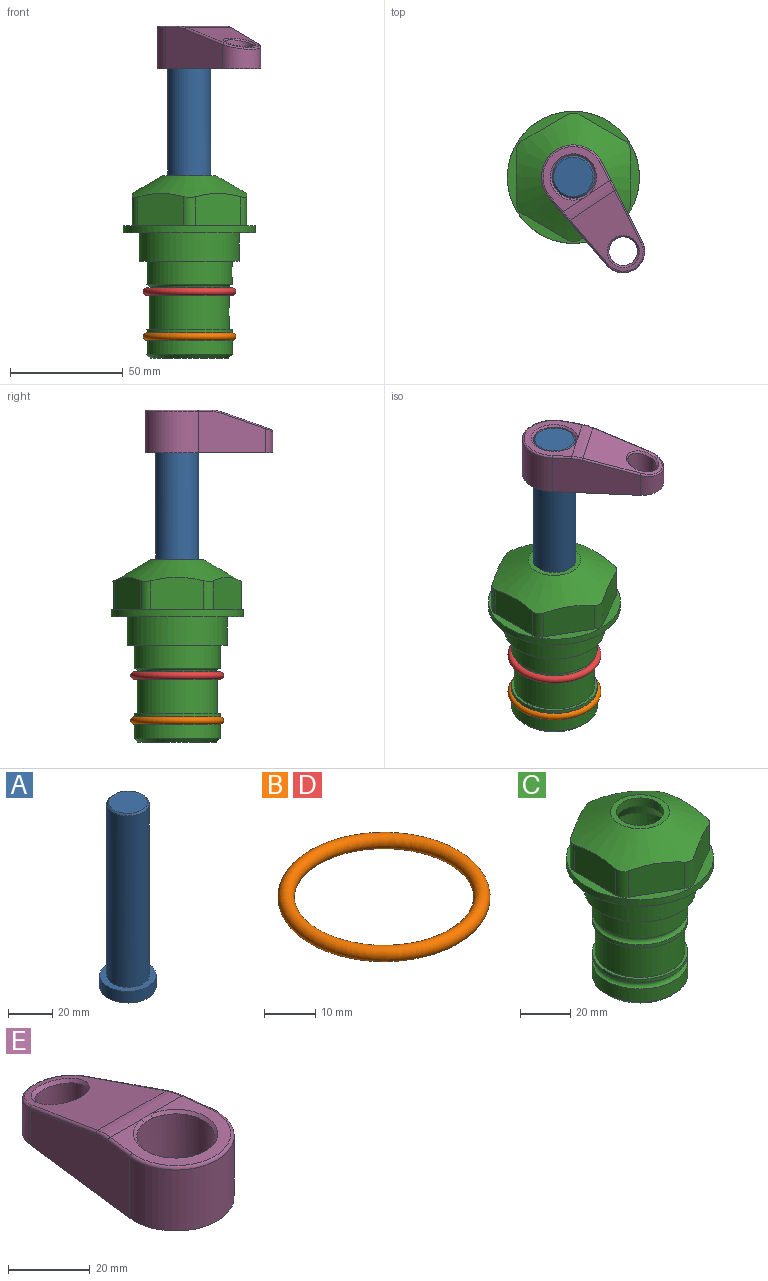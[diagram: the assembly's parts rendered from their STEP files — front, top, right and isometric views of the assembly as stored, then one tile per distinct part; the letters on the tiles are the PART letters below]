
ASSEMBLY  parts=5 mates=4
PART A: 6 faces, bbox 25.4x25.4x101.6 mm
  f0: plane 17.46x17.46mm, normal (0,0,1), area 239.5mm2, adj f5
  f1: plane 25.4x25.4mm, normal (0,0,-1), area 506.7mm2, adj f2
  f2: cylinder r=12.7mm len=25.4mm, axis (0,0,1), area 506.7mm2, adj f1,f3
  f3: plane 25.4x25.4mm, normal (0,0,1), area 221.7mm2, adj f2,f4
  f4: cylinder r=9.53mm len=94.46mm, axis (0,0,1), area 5653mm2, adj f3,f5
  f5: cone r=8.73mm half-angle=45deg, axis (0,0,-1), area 64.4mm2, adj f0,f4
PART B: 1 faces, bbox 44.7x44.7x3.2 mm
  f0: torus R=19.05mm, axis (0,0,1), area 1193.9mm2
PART C: 36 faces, bbox 58.7x58.7x81 mm
  f0: cylinder r=17.78mm len=35.56mm, axis (0,0,1), area 1670.8mm2, adj f23,f24,f31
  f1: cylinder r=19.05mm len=38.1mm, axis (0,0,1), area 1191.9mm2, adj f26,f27,f30
  f2: plane 58.66x58.66mm, normal (0,0,-1), area 1150.6mm2, adj f3,f28
  f3: cylinder r=29.33mm len=58.66mm, axis (0,0,-1), area 585.1mm2, adj f2,f4
  f4: plane 58.66x58.66mm, normal (0,0,1), area 475.9mm2, adj f3,f5,f6,f7,f8,f9,f10,f11
  f5: plane 20.32x14.34mm, normal (-0.5,0.87,0), area 324.4mm2, adj f4,f15,f16,f17
  f6: plane 20.32x14.34mm, normal (0.5,0.87,0), area 324.4mm2, adj f4,f14,f15,f17
  f7: plane 23.48x14.34mm, normal (1,0,0), area 324.4mm2, adj f4,f13,f14,f17
  f8: plane 20.32x14.34mm, normal (0.5,-0.87,0), area 324.4mm2, adj f4,f12,f13,f17
  f9: plane 20.32x14.34mm, normal (-0.5,-0.87,0), area 324.4mm2, adj f4,f11,f12,f17
  f10: plane 23.48x14.34mm, normal (-1,0,0), area 324.4mm2, adj f4,f11,f16,f17
  f11: cylinder r=5.08mm len=12.85mm, axis (0,0,-1), area 67.2mm2, adj f4,f9,f10,f17
  f12: cylinder r=5.08mm len=12.85mm, axis (0,0,-1), area 67.2mm2, adj f4,f8,f9,f17
  f13: cylinder r=5.08mm len=12.85mm, axis (0,0,-1), area 67.2mm2, adj f4,f7,f8,f17
  f14: cylinder r=5.08mm len=12.85mm, axis (0,0,-1), area 67.2mm2, adj f4,f6,f7,f17
  f15: cylinder r=5.08mm len=12.85mm, axis (0,0,-1), area 67.2mm2, adj f4,f5,f6,f17
  f16: cylinder r=5.08mm len=12.85mm, axis (0,0,-1), area 67.2mm2, adj f4,f5,f10,f17
  f17: cone r=11.73mm half-angle=60deg, axis (0,0,-1), area 2071.8mm2, adj f5,f6,f7,f8,f9,f10,f11,f12
  f18: plane 23.46x23.46mm, normal (0,0,1), area 147.4mm2, adj f17,f35
  f19: plane 34.93x34.93mm, normal (0,0,-1), area 958mm2, adj f29
  f20: cylinder r=19.05mm len=38.1mm, axis (0,0,1), area 760.1mm2, adj f21,f29
  f21: torus R=19.05mm, axis (0,0,1), area 565.3mm2, adj f20,f22
  f22: cylinder r=19.05mm len=38.1mm, axis (0,0,1), area 190mm2, adj f21,f23
  f23: plane 38.1x38.1mm, normal (0,0,1), area 146.9mm2, adj f0,f22
  f24: plane 38.1x38.1mm, normal (0,0,-1), area 146.9mm2, adj f0,f25
  f25: cylinder r=19.05mm len=38.1mm, axis (0,0,1), area 190mm2, adj f24,f26
  f26: torus R=19.05mm, axis (0,0,1), area 565.3mm2, adj f1,f25
  f27: plane 44.45x44.45mm, normal (0,0,-1), area 411.7mm2, adj f1,f28
  f28: cylinder r=22.23mm len=44.45mm, axis (0,0,1), area 1773.5mm2, adj f2,f27
  f29: cone r=19.05mm half-angle=45deg, axis (0,0,1), area 257.5mm2, adj f19,f20
  f30: cylinder r=3.17mm len=6.75mm, axis (-1,0,0), area 128mm2, adj f1,f33
  f31: cylinder r=3.17mm len=6.35mm, axis (-1,0,0), area 102.5mm2, adj f0,f33
  f32: plane 25.4x25.4mm, normal (0,0,1), area 506.7mm2, adj f33
  f33: cylinder r=12.7mm len=66.42mm, axis (0,0,-1), area 5236.2mm2, adj f30,f31,f32,f34
  f34: cone r=9.53mm half-angle=30deg, axis (0,0,-1), area 443.4mm2, adj f33,f35
  f35: cylinder r=9.53mm len=19.05mm, axis (0,0,-1), area 240.9mm2, adj f18,f34
PART D: same geometry as B
PART E: 31 faces, bbox 31.7x65.5x19.8 mm
  f0: plane 39.12x18.26mm, normal (0.99,0.12,0), area 612.2mm2, adj f1,f4,f7,f11,f13,f15
  f1: cylinder r=9.53mm len=18.91mm, axis (0,0,-1), area 296.1mm2, adj f0,f2,f7,f17
  f2: plane 39.12x18.26mm, normal (-0.99,0.12,0), area 612.2mm2, adj f1,f4,f7,f12,f14,f16
  f3: cylinder r=6.35mm len=12.7mm, axis (0,0,-1), area 362.4mm2, adj f7,f18
  f4: cylinder r=14.29mm len=28.58mm, axis (0,0,-1), area 882.2mm2, adj f0,f2,f7,f10
  f5: cylinder r=9.53mm len=19.05mm, axis (0,0,-1), area 1092.6mm2, adj f7,f19,f20
  f6: plane 26.99x23.69mm, normal (0,0,1), area 216.2mm2, adj f9,f10,f11,f12,f19
  f7: plane 63.5x28.58mm, normal (0,0,-1), area 661.8mm2, adj f0,f1,f2,f3,f4,f5,f22,f23
  f8: plane 33.52x23.6mm, normal (0,0.26,0.97), area 486mm2, adj f9,f15,f16,f17,f18
  f9: cylinder r=19.05mm len=24.72mm, axis (1,0,0), area 120.4mm2, adj f6,f8,f13,f14,f20
  f10: torus R=13.49mm, axis (0,0,1), area 59mm2, adj f4,f6,f11,f12
  f11: cylinder r=0.79mm len=8.67mm, axis (0.12,-0.99,0), area 10.8mm2, adj f0,f6,f10,f13
  f12: cylinder r=0.79mm len=8.67mm, axis (0.12,0.99,0), area 10.8mm2, adj f2,f6,f10,f14
  f13: bspline ~4.95x1.42mm, area 6.1mm2, adj f0,f9,f11,f15
  f14: bspline ~4.95x1.42mm, area 6.1mm2, adj f2,f9,f12,f16
  f15: cylinder r=0.79mm len=25.95mm, axis (0.12,-0.96,0.26), area 32.9mm2, adj f0,f8,f13,f17
  f16: cylinder r=0.79mm len=25.95mm, axis (0.12,0.96,-0.26), area 32.9mm2, adj f2,f8,f14,f17
  f17: bspline ~18.91x8.38mm, area 30mm2, adj f1,f8,f15,f16
  f18: bspline ~14.29x14.29mm, area 48.3mm2, adj f3,f8
  f19: cone r=9.53mm half-angle=45deg, axis (0,0,1), area 66.5mm2, adj f5,f6,f20
  f20: bspline ~3.22x0.96mm, area 3.5mm2, adj f5,f9,f19
  f21: plane 2.75x2.72mm, normal (0,0,-1), area 2.9mm2, adj f23,f25,f28
  f22: plane 23.05x15.88mm, normal (-0.99,-0.12,0), area 323.6mm2, adj f7,f25,f26,f27,f28,f29
  f23: plane 23.05x15.88mm, normal (0.99,-0.12,0), area 323.6mm2, adj f7,f21,f25,f27,f28,f30
  f24: cylinder r=9.53mm len=10.69mm, axis (0,0,-1), area 114.7mm2, adj f7,f27,f29,f30
  f25: cylinder r=12.7mm len=20.59mm, axis (0,0,-1), area 381.1mm2, adj f7,f21,f22,f23,f26,f28
  f26: plane 2.75x2.72mm, normal (0,0,-1), area 2.9mm2, adj f22,f25,f28
  f27: plane 19.72x18.37mm, normal (0,-0.26,-0.97), area 291.8mm2, adj f22,f23,f24,f28,f29,f30
  f28: cylinder r=15.88mm len=19.92mm, axis (1,0,0), area 54.8mm2, adj f21,f22,f23,f25,f26,f27
  f29: cylinder r=1.59mm len=11mm, axis (0,0,-1), area 34.7mm2, adj f7,f22,f24,f27
  f30: cylinder r=1.59mm len=11mm, axis (0,0,-1), area 34.7mm2, adj f7,f23,f24,f27
PLACE A rot(axis=(0,0,-1),146.1deg) t=(0,0,27.55)mm
PLACE B t=(0,0,-21.59)mm
PLACE C at identity fixed
PLACE D t=(0,0,-1.59)mm
PLACE E rot(axis=(0,0,-1),146.1deg) t=(0,0,28.35)mm
MATE cylindrical A.f2 <-> C.f0  axis (0,0,-1) through (0,0,-10.55)mm
MATE fastened E.f4 <-> A.f2  axis (0,0,-1) through (0,0,91.05)mm
MATE fastened D.f0 <-> C.f0  axis (0,0,1) through (0,0,-26.1)mm
MATE fastened B.f0 <-> C.f0  axis (0,0,1) through (0,0,-46.1)mm
